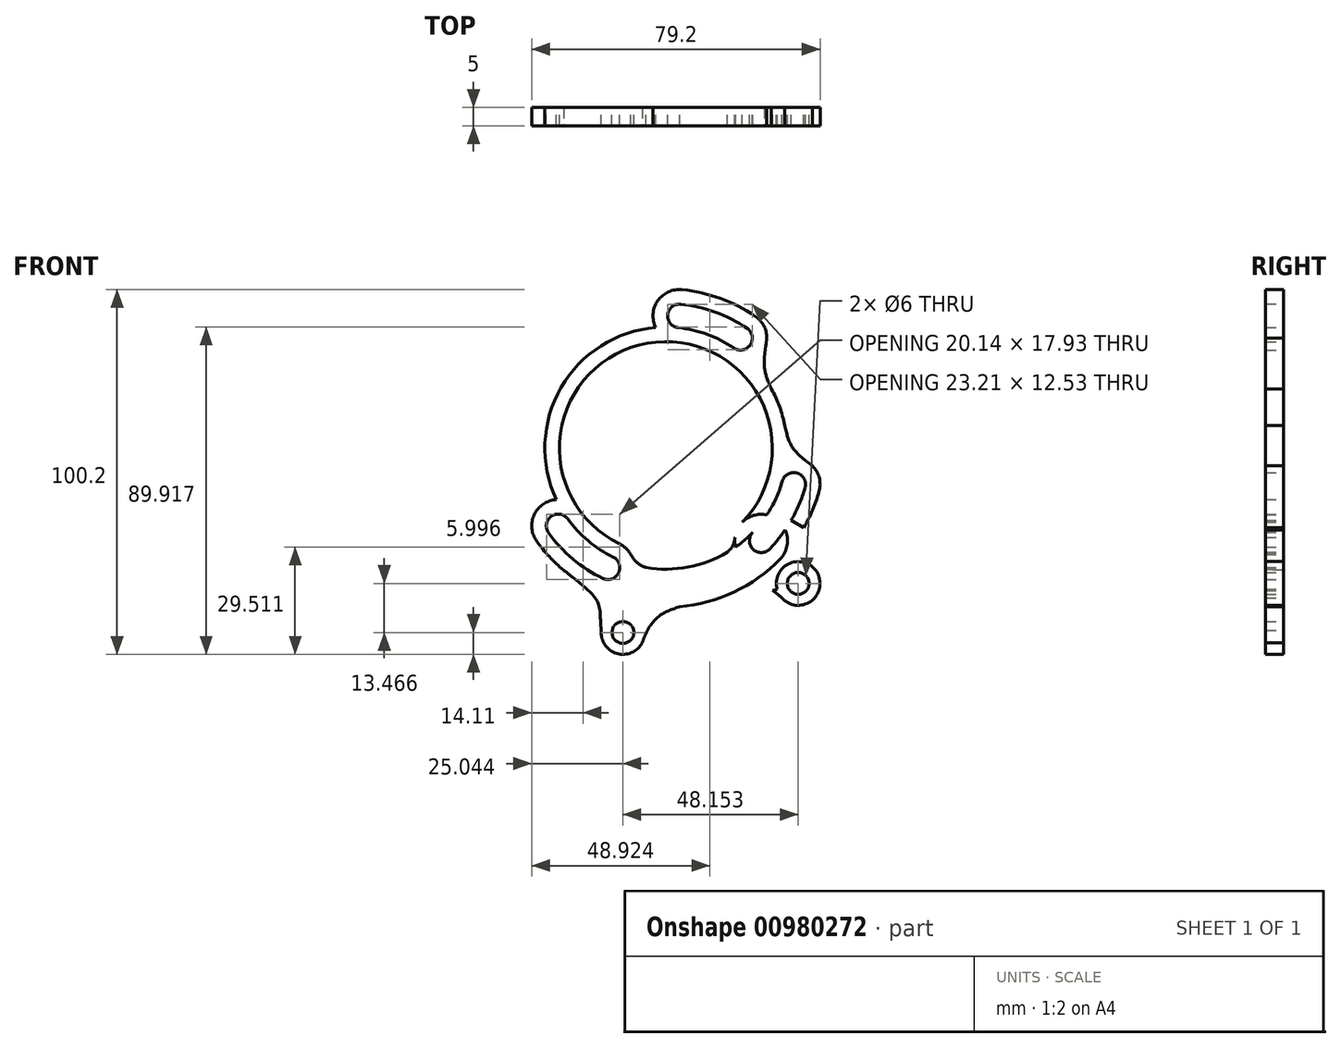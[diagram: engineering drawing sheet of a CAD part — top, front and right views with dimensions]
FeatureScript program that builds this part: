
annotation { "Feature Type Name" : "Feature", "Feature Type Description" : "" }
export const myFeature = defineFeature(function(context is Context, id is Id, definition is map)
    precondition{}
    {
        {
            var Q0;
            Q0=qCreatedBy(makeId("Front.planeOp"),FACE);
            var sketch = newSketch(context, id + "F0", { "sketchPlane" : qUnion([Q0])});
            skCircle(sketch, "E0", {"center": v(0, 0) * mm, "radius": 36.5 * mm});
            skCircle(sketch, "E1", {"center": v(-23.46, -27.96) * mm, "radius": 3.25 * mm});
            skCircle(sketch, "E2", {"center": v(31.6, -18.25) * mm, "radius": 3.25 * mm});
            skCircle(sketch, "E3", {"center": v(12.48, 34.3) * mm, "radius": 3.25 * mm});
            skLineSegment(sketch, "E4", {"start": v(0, 0) * mm, "end": v(-38.76, -46.2) * mm});
            skLineSegment(sketch, "E5", {"start": v(-38.76, -46.2) * mm, "end": v(0, 0) * mm});
            skLineSegment(sketch, "E6", {"start": v(0, 0) * mm, "end": v(58.35, -33.69) * mm});
            skLineSegment(sketch, "E7", {"start": v(58.35, -33.69) * mm, "end": v(0, 0) * mm});
            skLineSegment(sketch, "E8", {"start": v(0, 0) * mm, "end": v(16.1, 44.25) * mm});
            skCircle(sketch, "E9", {"center": v(3.71, 36.31) * mm, "radius": 3.25 * mm});
            skCircle(sketch, "E10", {"center": v(20.5, 30.2) * mm, "radius": 3.25 * mm});
            skCircle(sketch, "E11", {"center": v(35.11, -9.96) * mm, "radius": 3.25 * mm});
            skCircle(sketch, "E12", {"center": v(26.18, -25.43) * mm, "radius": 3.25 * mm});
            skCircle(sketch, "E13", {"center": v(-15.9, -32.85) * mm, "radius": 3.25 * mm});
            skCircle(sketch, "E14", {"center": v(-29.6, -21.37) * mm, "radius": 3.25 * mm});
            skLineSegment(sketch, "E15", {"start": v(-29.6, -21.37) * mm, "end": v(-23.46, -27.96) * mm});
            skLineSegment(sketch, "E16", {"start": v(-23.46, -27.96) * mm, "end": v(-15.9, -32.85) * mm});
            skLineSegment(sketch, "E17", {"start": v(26.18, -25.43) * mm, "end": v(31.6, -18.25) * mm});
            skLineSegment(sketch, "E18", {"start": v(35.11, -9.96) * mm, "end": v(31.6, -18.25) * mm});
            skLineSegment(sketch, "E19", {"start": v(12.48, 34.3) * mm, "end": v(20.5, 30.2) * mm});
            skLineSegment(sketch, "E20", {"start": v(12.48, 34.3) * mm, "end": v(3.71, 36.31) * mm});
            skCircle(sketch, "E21", {"center": v(0, 0) * mm, "radius": 33.25 * mm});
            skCircle(sketch, "E22", {"center": v(0, 0) * mm, "radius": 39.75 * mm});
            skCircle(sketch, "E23", {"center": v(0, 0) * mm, "radius": 29.25 * mm});
            skCircle(sketch, "E24", {"center": v(0, 0) * mm, "radius": 43.75 * mm});
            skCircle(sketch, "E25", {"center": v(3.71, 36.31) * mm, "radius": 7.25 * mm});
            skCircle(sketch, "E26", {"center": v(-29.6, -21.37) * mm, "radius": 7.25 * mm});
            skCircle(sketch, "E27", {"center": v(-15.9, -32.85) * mm, "radius": 7.25 * mm});
            skCircle(sketch, "E28", {"center": v(26.18, -25.43) * mm, "radius": 7.25 * mm});
            skCircle(sketch, "E29", {"center": v(35.11, -9.96) * mm, "radius": 7.25 * mm});
            skCircle(sketch, "E30", {"center": v(20.5, 30.2) * mm, "radius": 7.25 * mm});
            skCircle(sketch, "E31", {"center": v(0, 0) * mm, "radius": 52 * mm});
            skCircle(sketch, "E32", {"center": v(-11.8, -50.64) * mm, "radius": 3 * mm});
            skCircle(sketch, "E33", {"center": v(-11.8, -50.64) * mm, "radius": 6 * mm});
            skCircle(sketch, "E34", {"center": v(36.36, -37.18) * mm, "radius": 3 * mm});
            skCircle(sketch, "E35", {"center": v(36.36, -37.18) * mm, "radius": 6 * mm});
            skLineSegment(sketch, "E36", {"start": v(-11.8, -50.64) * mm, "end": v(36.36, -37.18) * mm});
            skFitSpline(sketch, "E37", {"points": [v(-17.77, -50.08) * mm, v(-28.12, -33.51) * mm], "startDerivative": vector(-2.15, 24.86) * mm, "endDerivative": vector(-34.83, 26.96) * mm});
            skFitSpline(sketch, "E38", {"points": [v(-6.5, -53.46) * mm, v(3.76, -43.59) * mm], "startDerivative": vector(7, 19.86) * mm, "endDerivative": vector(16.08, 4.93) * mm});
            skFitSpline(sketch, "E39", {"points": [v(31.83, -41.12) * mm, v(20.07, -38.88) * mm], "startDerivative": vector(-11.97, 10.58) * mm, "endDerivative": vector(-20.52, -5.17) * mm});
            skFitSpline(sketch, "E40", {"points": [v(40.4, -32.74) * mm, v(39.4, -19) * mm], "startDerivative": vector(-8.21, 10.84) * mm, "endDerivative": vector(10.07, 24.3) * mm});
            skFitSpline(sketch, "E41", {"points": [v(-9.62, -29.24) * mm, v(-5.43, -32.8) * mm], "startDerivative": vector(3.56, -5.9) * mm, "endDerivative": vector(6.8, -2.28) * mm});
            skFitSpline(sketch, "E42", {"points": [v(19, -24.5) * mm, v(16.88, -28.65) * mm], "startDerivative": vector(-0.78, -6.28) * mm, "endDerivative": vector(-4.07, -3.91) * mm});
            skFitSpline(sketch, "E43", {"points": [v(27.75, 30.27) * mm, v(29, 16.25) * mm], "startDerivative": vector(-3.36, -22.5) * mm, "endDerivative": vector(7.15, -15.45) * mm});
            skFitSpline(sketch, "E44", {"points": [v(40.2, -4.8) * mm, v(32.67, 6.19) * mm], "startDerivative": vector(-16.22, 11.75) * mm, "endDerivative": vector(-3.55, 16.52) * mm});
            skCircle(sketch, "E45", {"center": v(0, 0) * mm, "radius": 63 * mm});
            skCircle(sketch, "E46", {"center": v(6.41, -62.67) * mm, "radius": 3 * mm});
            skCircle(sketch, "E47", {"center": v(6.41, -62.67) * mm, "radius": 6 * mm});
            skCircle(sketch, "E48", {"center": v(50.05, -38.26) * mm, "radius": 3 * mm});
            skCircle(sketch, "E49", {"center": v(50.05, -38.26) * mm, "radius": 6 * mm});
            skLineSegment(sketch, "E50", {"start": v(6.41, -62.67) * mm, "end": v(50.05, -38.26) * mm});
            skSolve(sketch);
        }
        {
            var Q0;
            {var subQ0=sQuery(id+"F0.wireOp",EDGE,"E22");var subQ1=makeQuery(id+"F0.imprint","INTERSECT",VERTEX,{"derivedFrom":[sQuery(id+"F0.wireOp",EDGE,"E14"),subQ0]});Q0=makeQuery(id+"F0.imprint","IMPRINT",FACE,{"disambiguationData":[TD([[makeQuery(id+"F0.imprint","IMPRINT",EDGE,{"disambiguationData":[TD([[subQ1,1.0]])],"derivedFrom":subQ0}),-1.0]])]});}
            var Q1;
            {var subQ0=sQuery(id+"F0.wireOp",EDGE,"E26");var subQ1=sQuery(id+"F0.wireOp",EDGE,"E0");var subQ2=makeQuery(id+"F0.imprint","INTERSECT",VERTEX,{"disambiguationData":[OD(0.0)],"derivedFrom":[subQ1,subQ0]});Q1=makeQuery(id+"F0.imprint","IMPRINT",FACE,{"disambiguationData":[TD([[makeQuery(id+"F0.imprint","IMPRINT",EDGE,{"disambiguationData":[TD([[subQ2,-1.0]])],"derivedFrom":subQ1}),-1.0]])]});}
            var Q2;
            {var subQ0=sQuery(id+"F0.wireOp",EDGE,"E26");var subQ1=sQuery(id+"F0.wireOp",EDGE,"E0");var subQ2=makeQuery(id+"F0.imprint","INTERSECT",VERTEX,{"disambiguationData":[OD(0.0)],"derivedFrom":[subQ1,subQ0]});Q2=makeQuery(id+"F0.imprint","IMPRINT",FACE,{"disambiguationData":[TD([[makeQuery(id+"F0.imprint","IMPRINT",EDGE,{"disambiguationData":[TD([[subQ2,-1.0]])],"derivedFrom":subQ1}),1.0]])]});}
            var Q3;
            {var subQ0=sQuery(id+"F0.wireOp",EDGE,"E21");var subQ1=makeQuery(id+"F0.imprint","INTERSECT",VERTEX,{"derivedFrom":[sQuery(id+"F0.wireOp",EDGE,"E14"),subQ0]});Q3=makeQuery(id+"F0.imprint","IMPRINT",FACE,{"disambiguationData":[TD([[makeQuery(id+"F0.imprint","IMPRINT",EDGE,{"disambiguationData":[TD([[subQ1,1.0]])],"derivedFrom":subQ0}),1.0]])]});}
            var Q4;
            {var subQ0=sQuery(id+"F0.wireOp",EDGE,"E23");var subQ1=sQuery(id+"F0.wireOp",EDGE,"E5");var subQ2=makeQuery(id+"F0.imprint","INTERSECT",VERTEX,{"derivedFrom":[subQ1,subQ0]});Q4=makeQuery(id+"F0.imprint","IMPRINT",FACE,{"disambiguationData":[TD([[makeQuery(id+"F0.imprint","IMPRINT",EDGE,{"disambiguationData":[TD([[subQ2,1.0]])],"derivedFrom":subQ0}),-1.0]])]});}
            var Q5;
            {var subQ0=sQuery(id+"F0.wireOp",EDGE,"E23");var subQ1=sQuery(id+"F0.wireOp",EDGE,"E5");var subQ2=makeQuery(id+"F0.imprint","INTERSECT",VERTEX,{"derivedFrom":[subQ1,subQ0]});Q5=makeQuery(id+"F0.imprint","IMPRINT",FACE,{"disambiguationData":[TD([[makeQuery(id+"F0.imprint","IMPRINT",EDGE,{"disambiguationData":[TD([[subQ2,-1.0]])],"derivedFrom":subQ0}),-1.0]])]});}
            var Q6;
            {var subQ3=sQuery(id+"F0.wireOp",EDGE,"E21");var subQ5=makeQuery(id+"F0.imprint","INTERSECT",VERTEX,{"derivedFrom":[sQuery(id+"F0.wireOp",EDGE,"E13"),subQ3]});Q6=makeQuery(id+"F0.imprint","IMPRINT",FACE,{"disambiguationData":[TD([[makeQuery(id+"F0.imprint","IMPRINT",EDGE,{"disambiguationData":[TD([[subQ5,1.0]])],"derivedFrom":subQ3}),1.0]])]});}
            var Q7;
            {var subQ0=sQuery(id+"F0.wireOp",EDGE,"E41");Q7=makeQuery(id+"F0.imprint","IMPRINT",FACE,{"disambiguationData":[TD([[makeQuery(id+"F0.imprint","IMPRINT",EDGE,{"derivedFrom":subQ0}),-1.0]])]});}
            var Q8;
            {var subQ3=sQuery(id+"F0.wireOp",EDGE,"E22");var subQ5=sQuery(id+"F0.wireOp",EDGE,"E26");var subQ6=makeQuery(id+"F0.imprint","INTERSECT",VERTEX,{"disambiguationData":[OD(1.0)],"derivedFrom":[subQ3,subQ5]});Q8=makeQuery(id+"F0.imprint","IMPRINT",FACE,{"disambiguationData":[TD([[makeQuery(id+"F0.imprint","IMPRINT",EDGE,{"disambiguationData":[TD([[subQ6,1.0]])],"derivedFrom":subQ5}),-1.0]])]});}
            var Q9;
            {var subQ3=sQuery(id+"F0.wireOp",EDGE,"E22");var subQ5=sQuery(id+"F0.wireOp",EDGE,"E27");var subQ6=makeQuery(id+"F0.imprint","INTERSECT",VERTEX,{"disambiguationData":[OD(0.0)],"derivedFrom":[subQ3,subQ5]});Q9=makeQuery(id+"F0.imprint","IMPRINT",FACE,{"disambiguationData":[TD([[makeQuery(id+"F0.imprint","IMPRINT",EDGE,{"disambiguationData":[TD([[subQ6,-1.0]])],"derivedFrom":subQ5}),-1.0]])]});}
            var Q10;
            {var subQ0=sQuery(id+"F0.wireOp",EDGE,"E33");var subQ1=sQuery(id+"F0.wireOp",EDGE,"E31");var subQ2=makeQuery(id+"F0.imprint","INTERSECT",VERTEX,{"disambiguationData":[OD(0.0)],"derivedFrom":[subQ1,subQ0]});Q10=makeQuery(id+"F0.imprint","IMPRINT",FACE,{"disambiguationData":[TD([[makeQuery(id+"F0.imprint","IMPRINT",EDGE,{"disambiguationData":[TD([[subQ2,-1.0]])],"derivedFrom":subQ1}),1.0]])]});}
            var Q11;
            {var subQ0=sQuery(id+"F0.wireOp",EDGE,"E33");var subQ2=sQuery(id+"F0.wireOp",EDGE,"E31");var subQ3=makeQuery(id+"F0.imprint","INTERSECT",VERTEX,{"disambiguationData":[OD(0.0)],"derivedFrom":[subQ2,subQ0]});Q11=makeQuery(id+"F0.imprint","IMPRINT",FACE,{"disambiguationData":[TD([[makeQuery(id+"F0.imprint","IMPRINT",EDGE,{"disambiguationData":[TD([[subQ3,-1.0]])],"derivedFrom":subQ2}),-1.0]])]});}
            var Q12;
            {var subQ0=sQuery(id+"F0.wireOp",EDGE,"E32");var subQ1=sQuery(id+"F0.wireOp",EDGE,"E31");var subQ2=makeQuery(id+"F0.imprint","INTERSECT",VERTEX,{"disambiguationData":[OD(1.0)],"derivedFrom":[subQ1,subQ0]});Q12=makeQuery(id+"F0.imprint","IMPRINT",FACE,{"disambiguationData":[TD([[makeQuery(id+"F0.imprint","IMPRINT",EDGE,{"disambiguationData":[TD([[subQ2,-1.0]])],"derivedFrom":subQ1}),1.0]])]});}
            var Q13;
            {var subQ5=sQuery(id+"F0.wireOp",EDGE,"E38");var subQ6=sQuery(id+"F0.wireOp",EDGE,"E24");var subQ7=makeQuery(id+"F0.imprint","INTERSECT",VERTEX,{"derivedFrom":[subQ6,subQ5]});Q13=makeQuery(id+"F0.imprint","IMPRINT",FACE,{"disambiguationData":[TD([[makeQuery(id+"F0.imprint","IMPRINT",EDGE,{"disambiguationData":[TD([[subQ7,1.0]])],"derivedFrom":subQ6}),-1.0]])]});}
            var Q14;
            {var subQ0=sQuery(id+"F0.wireOp",EDGE,"E37");var subQ1=sQuery(id+"F0.wireOp",EDGE,"E31");var subQ2=makeQuery(id+"F0.imprint","INTERSECT",VERTEX,{"derivedFrom":[subQ1,subQ0]});Q14=makeQuery(id+"F0.imprint","IMPRINT",FACE,{"disambiguationData":[TD([[makeQuery(id+"F0.imprint","IMPRINT",EDGE,{"disambiguationData":[TD([[subQ2,-1.0]])],"derivedFrom":subQ1}),-1.0]])]});}
            var Q15;
            {var subQ0=sQuery(id+"F0.wireOp",EDGE,"E38");var subQ1=sQuery(id+"F0.wireOp",EDGE,"E31");var subQ2=makeQuery(id+"F0.imprint","INTERSECT",VERTEX,{"derivedFrom":[subQ1,subQ0]});Q15=makeQuery(id+"F0.imprint","IMPRINT",FACE,{"disambiguationData":[TD([[makeQuery(id+"F0.imprint","IMPRINT",EDGE,{"disambiguationData":[TD([[subQ2,1.0]])],"derivedFrom":subQ1}),-1.0]])]});}
            var Q16;
            {var subQ0=sQuery(id+"F0.wireOp",EDGE,"E38");var subQ1=sQuery(id+"F0.wireOp",EDGE,"E31");var subQ2=makeQuery(id+"F0.imprint","INTERSECT",VERTEX,{"derivedFrom":[subQ1,subQ0]});Q16=makeQuery(id+"F0.imprint","IMPRINT",FACE,{"disambiguationData":[TD([[makeQuery(id+"F0.imprint","IMPRINT",EDGE,{"disambiguationData":[TD([[subQ2,1.0]])],"derivedFrom":subQ1}),1.0]])]});}
            var Q17;
            {var subQ3=sQuery(id+"F0.wireOp",EDGE,"E27");var subQ7=sQuery(id+"F0.wireOp",EDGE,"E22");var subQ8=makeQuery(id+"F0.imprint","INTERSECT",VERTEX,{"disambiguationData":[OD(1.0)],"derivedFrom":[subQ7,subQ3]});Q17=makeQuery(id+"F0.imprint","IMPRINT",FACE,{"disambiguationData":[TD([[makeQuery(id+"F0.imprint","IMPRINT",EDGE,{"disambiguationData":[TD([[subQ8,-1.0]])],"derivedFrom":subQ7}),-1.0]])]});}
            var Q18;
            {var subQ0=sQuery(id+"F0.wireOp",EDGE,"E22");var subQ1=makeQuery(id+"F0.imprint","INTERSECT",VERTEX,{"derivedFrom":[sQuery(id+"F0.wireOp",EDGE,"E13"),subQ0]});Q18=makeQuery(id+"F0.imprint","IMPRINT",FACE,{"disambiguationData":[TD([[makeQuery(id+"F0.imprint","IMPRINT",EDGE,{"disambiguationData":[TD([[subQ1,1.0]])],"derivedFrom":subQ0}),-1.0]])]});}
            var Q19;
            {var subQ5=sQuery(id+"F0.wireOp",EDGE,"E27");var subQ7=sQuery(id+"F0.wireOp",EDGE,"E0");var subQ8=makeQuery(id+"F0.imprint","INTERSECT",VERTEX,{"disambiguationData":[OD(1.0)],"derivedFrom":[subQ7,subQ5]});Q19=makeQuery(id+"F0.imprint","IMPRINT",FACE,{"disambiguationData":[TD([[makeQuery(id+"F0.imprint","IMPRINT",EDGE,{"disambiguationData":[TD([[subQ8,-1.0]])],"derivedFrom":subQ7}),1.0]])]});}
            var Q20;
            {var subQ0=sQuery(id+"F0.wireOp",EDGE,"E27");var subQ1=sQuery(id+"F0.wireOp",EDGE,"E0");var subQ2=makeQuery(id+"F0.imprint","INTERSECT",VERTEX,{"disambiguationData":[OD(1.0)],"derivedFrom":[subQ1,subQ0]});Q20=makeQuery(id+"F0.imprint","IMPRINT",FACE,{"disambiguationData":[TD([[makeQuery(id+"F0.imprint","IMPRINT",EDGE,{"disambiguationData":[TD([[subQ2,-1.0]])],"derivedFrom":subQ1}),-1.0]])]});}
            var Q21;
            {var subQ0=sQuery(id+"F0.wireOp",EDGE,"E13");var subQ1=sQuery(id+"F0.wireOp",EDGE,"E0");var subQ2=makeQuery(id+"F0.imprint","INTERSECT",VERTEX,{"disambiguationData":[OD(1.0)],"derivedFrom":[subQ1,subQ0]});Q21=makeQuery(id+"F0.imprint","IMPRINT",FACE,{"disambiguationData":[TD([[makeQuery(id+"F0.imprint","IMPRINT",EDGE,{"disambiguationData":[TD([[subQ2,-1.0]])],"derivedFrom":subQ1}),1.0]])]});}
            var Q22;
            {var subQ0=sQuery(id+"F0.wireOp",EDGE,"E13");var subQ1=sQuery(id+"F0.wireOp",EDGE,"E0");var subQ2=makeQuery(id+"F0.imprint","INTERSECT",VERTEX,{"disambiguationData":[OD(1.0)],"derivedFrom":[subQ1,subQ0]});Q22=makeQuery(id+"F0.imprint","IMPRINT",FACE,{"disambiguationData":[TD([[makeQuery(id+"F0.imprint","IMPRINT",EDGE,{"disambiguationData":[TD([[subQ2,-1.0]])],"derivedFrom":subQ1}),-1.0]])]});}
            var Q23;
            {var subQ0=sQuery(id+"F0.wireOp",EDGE,"E40");var subQ6=sQuery(id+"F0.wireOp",EDGE,"E7");var subQ11=makeQuery(id+"F0.imprint","INTERSECT",VERTEX,{"derivedFrom":[subQ6,subQ0]});Q23=makeQuery(id+"F0.imprint","IMPRINT",FACE,{"disambiguationData":[TD([[makeQuery(id+"F0.imprint","IMPRINT",EDGE,{"disambiguationData":[TD([[subQ11,-1.0]])],"derivedFrom":subQ6}),1.0]])]});}
            var Q24;
            {var subQ0=sQuery(id+"F0.wireOp",EDGE,"E42");Q24=makeQuery(id+"F0.imprint","IMPRINT",FACE,{"disambiguationData":[TD([[makeQuery(id+"F0.imprint","IMPRINT",EDGE,{"derivedFrom":subQ0}),1.0]])]});}
            var Q25;
            {var subQ0=sQuery(id+"F0.wireOp",EDGE,"E28");var subQ1=makeQuery(id+"F0.imprint","IMPRINT",VERTEX,{"derivedFrom":subQ0});Q25=makeQuery(id+"F0.imprint","IMPRINT",FACE,{"disambiguationData":[TD([[makeQuery(id+"F0.imprint","IMPRINT",EDGE,{"disambiguationData":[TD([[subQ1,1.0]])],"derivedFrom":subQ0}),1.0]])]});}
            var Q26;
            {var subQ0=sQuery(id+"F0.wireOp",EDGE,"E28");var subQ1=sQuery(id+"F0.wireOp",EDGE,"E0");var subQ2=makeQuery(id+"F0.imprint","INTERSECT",VERTEX,{"disambiguationData":[OD(0.0)],"derivedFrom":[subQ1,subQ0]});Q26=makeQuery(id+"F0.imprint","IMPRINT",FACE,{"disambiguationData":[TD([[makeQuery(id+"F0.imprint","IMPRINT",EDGE,{"disambiguationData":[TD([[subQ2,-1.0]])],"derivedFrom":subQ1}),1.0]])]});}
            var Q27;
            {var subQ0=sQuery(id+"F0.wireOp",EDGE,"E28");var subQ1=sQuery(id+"F0.wireOp",EDGE,"E0");var subQ2=makeQuery(id+"F0.imprint","INTERSECT",VERTEX,{"disambiguationData":[OD(0.0)],"derivedFrom":[subQ1,subQ0]});Q27=makeQuery(id+"F0.imprint","IMPRINT",FACE,{"disambiguationData":[TD([[makeQuery(id+"F0.imprint","IMPRINT",EDGE,{"disambiguationData":[TD([[subQ2,-1.0]])],"derivedFrom":subQ1}),-1.0]])]});}
            var Q28;
            {var subQ0=sQuery(id+"F0.wireOp",EDGE,"E22");var subQ1=makeQuery(id+"F0.imprint","INTERSECT",VERTEX,{"derivedFrom":[sQuery(id+"F0.wireOp",EDGE,"E12"),subQ0]});Q28=makeQuery(id+"F0.imprint","IMPRINT",FACE,{"disambiguationData":[TD([[makeQuery(id+"F0.imprint","IMPRINT",EDGE,{"disambiguationData":[TD([[subQ1,1.0]])],"derivedFrom":subQ0}),-1.0]])]});}
            var Q29;
            {var subQ1=sQuery(id+"F0.wireOp",EDGE,"E31");var subQ3=sQuery(id+"F0.wireOp",EDGE,"E34");var subQ4=makeQuery(id+"F0.imprint","INTERSECT",VERTEX,{"disambiguationData":[OD(1.0)],"derivedFrom":[subQ1,subQ3]});Q29=makeQuery(id+"F0.imprint","IMPRINT",FACE,{"disambiguationData":[TD([[makeQuery(id+"F0.imprint","IMPRINT",EDGE,{"disambiguationData":[TD([[subQ4,-1.0]])],"derivedFrom":subQ3}),-1.0]])]});}
            var Q30;
            {var subQ1=sQuery(id+"F0.wireOp",EDGE,"E31");var subQ3=sQuery(id+"F0.wireOp",EDGE,"E34");var subQ4=makeQuery(id+"F0.imprint","INTERSECT",VERTEX,{"disambiguationData":[OD(0.0)],"derivedFrom":[subQ1,subQ3]});Q30=makeQuery(id+"F0.imprint","IMPRINT",FACE,{"disambiguationData":[TD([[makeQuery(id+"F0.imprint","IMPRINT",EDGE,{"disambiguationData":[TD([[subQ4,-1.0]])],"derivedFrom":subQ3}),-1.0]])]});}
            var Q31;
            {var subQ0=sQuery(id+"F0.wireOp",EDGE,"E24");var subQ1=sQuery(id+"F0.wireOp",EDGE,"E7");var subQ2=makeQuery(id+"F0.imprint","INTERSECT",VERTEX,{"derivedFrom":[subQ1,subQ0]});Q31=makeQuery(id+"F0.imprint","IMPRINT",FACE,{"disambiguationData":[TD([[makeQuery(id+"F0.imprint","IMPRINT",EDGE,{"disambiguationData":[TD([[subQ2,1.0]])],"derivedFrom":subQ0}),1.0]])]});}
            var Q32;
            {var subQ0=sQuery(id+"F0.wireOp",EDGE,"E24");var subQ1=makeQuery(id+"F0.imprint","INTERSECT",VERTEX,{"derivedFrom":[subQ0,sQuery(id+"F0.wireOp",EDGE,"E40")]});Q32=makeQuery(id+"F0.imprint","IMPRINT",FACE,{"disambiguationData":[TD([[makeQuery(id+"F0.imprint","IMPRINT",EDGE,{"disambiguationData":[TD([[subQ1,1.0]])],"derivedFrom":subQ0}),1.0]])]});}
            var Q33;
            {var subQ0=sQuery(id+"F0.wireOp",EDGE,"E23");var subQ1=sQuery(id+"F0.wireOp",EDGE,"E7");var subQ2=makeQuery(id+"F0.imprint","INTERSECT",VERTEX,{"derivedFrom":[subQ1,subQ0]});Q33=makeQuery(id+"F0.imprint","IMPRINT",FACE,{"disambiguationData":[TD([[makeQuery(id+"F0.imprint","IMPRINT",EDGE,{"disambiguationData":[TD([[subQ2,1.0]])],"derivedFrom":subQ0}),-1.0]])]});}
            var Q34;
            {var subQ0=sQuery(id+"F0.wireOp",EDGE,"E23");var subQ1=sQuery(id+"F0.wireOp",EDGE,"E7");var subQ2=makeQuery(id+"F0.imprint","INTERSECT",VERTEX,{"derivedFrom":[subQ1,subQ0]});Q34=makeQuery(id+"F0.imprint","IMPRINT",FACE,{"disambiguationData":[TD([[makeQuery(id+"F0.imprint","IMPRINT",EDGE,{"disambiguationData":[TD([[subQ2,-1.0]])],"derivedFrom":subQ0}),-1.0]])]});}
            var Q35;
            {var subQ1=sQuery(id+"F0.wireOp",EDGE,"E31");var subQ3=sQuery(id+"F0.wireOp",EDGE,"E34");var subQ4=makeQuery(id+"F0.imprint","INTERSECT",VERTEX,{"disambiguationData":[OD(0.0)],"derivedFrom":[subQ1,subQ3]});Q35=makeQuery(id+"F0.imprint","IMPRINT",FACE,{"disambiguationData":[TD([[makeQuery(id+"F0.imprint","IMPRINT",EDGE,{"disambiguationData":[TD([[subQ4,1.0]])],"derivedFrom":subQ3}),-1.0]])]});}
            var Q36;
            {var subQ1=sQuery(id+"F0.wireOp",EDGE,"E35");var subQ3=sQuery(id+"F0.wireOp",EDGE,"E36");var subQ4=makeQuery(id+"F0.imprint","INTERSECT",VERTEX,{"derivedFrom":[subQ1,subQ3]});Q36=makeQuery(id+"F0.imprint","IMPRINT",FACE,{"disambiguationData":[TD([[makeQuery(id+"F0.imprint","IMPRINT",EDGE,{"disambiguationData":[TD([[subQ4,1.0]])],"derivedFrom":subQ3}),-1.0]])]});}
            var Q37;
            {var subQ0=sQuery(id+"F0.wireOp",EDGE,"E40");var subQ1=sQuery(id+"F0.wireOp",EDGE,"E7");var subQ2=makeQuery(id+"F0.imprint","INTERSECT",VERTEX,{"derivedFrom":[subQ1,subQ0]});Q37=makeQuery(id+"F0.imprint","IMPRINT",FACE,{"disambiguationData":[TD([[makeQuery(id+"F0.imprint","IMPRINT",EDGE,{"disambiguationData":[TD([[subQ2,-1.0]])],"derivedFrom":subQ1}),-1.0]])]});}
            var Q38;
            {var subQ1=sQuery(id+"F0.wireOp",EDGE,"E22");var subQ8=makeQuery(id+"F0.imprint","INTERSECT",VERTEX,{"derivedFrom":[sQuery(id+"F0.wireOp",EDGE,"E11"),subQ1]});Q38=makeQuery(id+"F0.imprint","IMPRINT",FACE,{"disambiguationData":[TD([[makeQuery(id+"F0.imprint","IMPRINT",EDGE,{"disambiguationData":[TD([[subQ8,1.0]])],"derivedFrom":subQ1}),-1.0]])]});}
            var Q39;
            {var subQ0=sQuery(id+"F0.wireOp",EDGE,"E11");var subQ1=sQuery(id+"F0.wireOp",EDGE,"E0");var subQ2=makeQuery(id+"F0.imprint","INTERSECT",VERTEX,{"disambiguationData":[OD(1.0)],"derivedFrom":[subQ1,subQ0]});Q39=makeQuery(id+"F0.imprint","IMPRINT",FACE,{"disambiguationData":[TD([[makeQuery(id+"F0.imprint","IMPRINT",EDGE,{"disambiguationData":[TD([[subQ2,-1.0]])],"derivedFrom":subQ1}),-1.0]])]});}
            var Q40;
            {var subQ0=sQuery(id+"F0.wireOp",EDGE,"E11");var subQ1=sQuery(id+"F0.wireOp",EDGE,"E0");var subQ2=makeQuery(id+"F0.imprint","INTERSECT",VERTEX,{"disambiguationData":[OD(1.0)],"derivedFrom":[subQ1,subQ0]});Q40=makeQuery(id+"F0.imprint","IMPRINT",FACE,{"disambiguationData":[TD([[makeQuery(id+"F0.imprint","IMPRINT",EDGE,{"disambiguationData":[TD([[subQ2,-1.0]])],"derivedFrom":subQ1}),1.0]])]});}
            var Q41;
            {var subQ0=sQuery(id+"F0.wireOp",EDGE,"E21");var subQ1=makeQuery(id+"F0.imprint","INTERSECT",VERTEX,{"derivedFrom":[sQuery(id+"F0.wireOp",EDGE,"E11"),subQ0]});Q41=makeQuery(id+"F0.imprint","IMPRINT",FACE,{"disambiguationData":[TD([[makeQuery(id+"F0.imprint","IMPRINT",EDGE,{"disambiguationData":[TD([[subQ1,1.0]])],"derivedFrom":subQ0}),1.0]])]});}
            var Q42;
            {var subQ0=sQuery(id+"F0.wireOp",EDGE,"E30");var subQ1=sQuery(id+"F0.wireOp",EDGE,"E21");var subQ2=makeQuery(id+"F0.imprint","INTERSECT",VERTEX,{"disambiguationData":[OD(0.0)],"derivedFrom":[subQ1,subQ0]});Q42=makeQuery(id+"F0.imprint","IMPRINT",FACE,{"disambiguationData":[TD([[makeQuery(id+"F0.imprint","IMPRINT",EDGE,{"disambiguationData":[TD([[subQ2,1.0]])],"derivedFrom":subQ1}),1.0]])]});}
            var Q43;
            {var subQ2=sQuery(id+"F0.wireOp",EDGE,"E22");var subQ6=makeQuery(id+"F0.imprint","INTERSECT",VERTEX,{"derivedFrom":[sQuery(id+"F0.wireOp",EDGE,"E10"),subQ2]});Q43=makeQuery(id+"F0.imprint","IMPRINT",FACE,{"disambiguationData":[TD([[makeQuery(id+"F0.imprint","IMPRINT",EDGE,{"disambiguationData":[TD([[subQ6,1.0]])],"derivedFrom":subQ2}),-1.0]])]});}
            var Q44;
            {var subQ0=sQuery(id+"F0.wireOp",EDGE,"E30");var subQ1=sQuery(id+"F0.wireOp",EDGE,"E0");var subQ2=makeQuery(id+"F0.imprint","INTERSECT",VERTEX,{"disambiguationData":[OD(0.0)],"derivedFrom":[subQ1,subQ0]});Q44=makeQuery(id+"F0.imprint","IMPRINT",FACE,{"disambiguationData":[TD([[makeQuery(id+"F0.imprint","IMPRINT",EDGE,{"disambiguationData":[TD([[subQ2,-1.0]])],"derivedFrom":subQ1}),-1.0]])]});}
            var Q45;
            {var subQ0=sQuery(id+"F0.wireOp",EDGE,"E30");var subQ1=sQuery(id+"F0.wireOp",EDGE,"E0");var subQ2=makeQuery(id+"F0.imprint","INTERSECT",VERTEX,{"disambiguationData":[OD(0.0)],"derivedFrom":[subQ1,subQ0]});Q45=makeQuery(id+"F0.imprint","IMPRINT",FACE,{"disambiguationData":[TD([[makeQuery(id+"F0.imprint","IMPRINT",EDGE,{"disambiguationData":[TD([[subQ2,-1.0]])],"derivedFrom":subQ1}),1.0]])]});}
            var Q46;
            {var subQ0=sQuery(id+"F0.wireOp",EDGE,"E21");var subQ1=makeQuery(id+"F0.imprint","INTERSECT",VERTEX,{"derivedFrom":[sQuery(id+"F0.wireOp",EDGE,"E10"),subQ0]});Q46=makeQuery(id+"F0.imprint","IMPRINT",FACE,{"disambiguationData":[TD([[makeQuery(id+"F0.imprint","IMPRINT",EDGE,{"disambiguationData":[TD([[subQ1,1.0]])],"derivedFrom":subQ0}),1.0]])]});}
            var Q47;
            {var subQ0=sQuery(id+"F0.wireOp",EDGE,"E23");var subQ1=sQuery(id+"F0.wireOp",EDGE,"E8");var subQ2=makeQuery(id+"F0.imprint","INTERSECT",VERTEX,{"derivedFrom":[subQ1,subQ0]});Q47=makeQuery(id+"F0.imprint","IMPRINT",FACE,{"disambiguationData":[TD([[makeQuery(id+"F0.imprint","IMPRINT",EDGE,{"disambiguationData":[TD([[subQ2,1.0]])],"derivedFrom":subQ0}),-1.0]])]});}
            var Q48;
            {var subQ0=sQuery(id+"F0.wireOp",EDGE,"E23");var subQ1=sQuery(id+"F0.wireOp",EDGE,"E8");var subQ2=makeQuery(id+"F0.imprint","INTERSECT",VERTEX,{"derivedFrom":[subQ1,subQ0]});Q48=makeQuery(id+"F0.imprint","IMPRINT",FACE,{"disambiguationData":[TD([[makeQuery(id+"F0.imprint","IMPRINT",EDGE,{"disambiguationData":[TD([[subQ2,-1.0]])],"derivedFrom":subQ0}),-1.0]])]});}
            var Q49;
            {var subQ0=sQuery(id+"F0.wireOp",EDGE,"E21");var subQ1=makeQuery(id+"F0.imprint","INTERSECT",VERTEX,{"derivedFrom":[sQuery(id+"F0.wireOp",EDGE,"E9"),subQ0]});Q49=makeQuery(id+"F0.imprint","IMPRINT",FACE,{"disambiguationData":[TD([[makeQuery(id+"F0.imprint","IMPRINT",EDGE,{"disambiguationData":[TD([[subQ1,1.0]])],"derivedFrom":subQ0}),1.0]])]});}
            var Q50;
            {var subQ0=sQuery(id+"F0.wireOp",EDGE,"E9");var subQ1=sQuery(id+"F0.wireOp",EDGE,"E0");var subQ2=makeQuery(id+"F0.imprint","INTERSECT",VERTEX,{"disambiguationData":[OD(1.0)],"derivedFrom":[subQ1,subQ0]});Q50=makeQuery(id+"F0.imprint","IMPRINT",FACE,{"disambiguationData":[TD([[makeQuery(id+"F0.imprint","IMPRINT",EDGE,{"disambiguationData":[TD([[subQ2,-1.0]])],"derivedFrom":subQ1}),1.0]])]});}
            var Q51;
            {var subQ0=sQuery(id+"F0.wireOp",EDGE,"E9");var subQ1=sQuery(id+"F0.wireOp",EDGE,"E0");var subQ2=makeQuery(id+"F0.imprint","INTERSECT",VERTEX,{"disambiguationData":[OD(1.0)],"derivedFrom":[subQ1,subQ0]});Q51=makeQuery(id+"F0.imprint","IMPRINT",FACE,{"disambiguationData":[TD([[makeQuery(id+"F0.imprint","IMPRINT",EDGE,{"disambiguationData":[TD([[subQ2,-1.0]])],"derivedFrom":subQ1}),-1.0]])]});}
            var Q52;
            {var subQ0=sQuery(id+"F0.wireOp",EDGE,"E22");var subQ1=makeQuery(id+"F0.imprint","INTERSECT",VERTEX,{"derivedFrom":[sQuery(id+"F0.wireOp",EDGE,"E9"),subQ0]});Q52=makeQuery(id+"F0.imprint","IMPRINT",FACE,{"disambiguationData":[TD([[makeQuery(id+"F0.imprint","IMPRINT",EDGE,{"disambiguationData":[TD([[subQ1,1.0]])],"derivedFrom":subQ0}),-1.0]])]});}
            var Q53;
            {var subQ0=sQuery(id+"F0.wireOp",EDGE,"E24");var subQ1=sQuery(id+"F0.wireOp",EDGE,"E8");var subQ2=makeQuery(id+"F0.imprint","INTERSECT",VERTEX,{"derivedFrom":[subQ1,subQ0]});Q53=makeQuery(id+"F0.imprint","IMPRINT",FACE,{"disambiguationData":[TD([[makeQuery(id+"F0.imprint","IMPRINT",EDGE,{"disambiguationData":[TD([[subQ2,-1.0]])],"derivedFrom":subQ0}),1.0]])]});}
            var Q54;
            {var subQ0=sQuery(id+"F0.wireOp",EDGE,"E24");var subQ1=sQuery(id+"F0.wireOp",EDGE,"E8");var subQ2=makeQuery(id+"F0.imprint","INTERSECT",VERTEX,{"derivedFrom":[subQ1,subQ0]});Q54=makeQuery(id+"F0.imprint","IMPRINT",FACE,{"disambiguationData":[TD([[makeQuery(id+"F0.imprint","IMPRINT",EDGE,{"disambiguationData":[TD([[subQ2,1.0]])],"derivedFrom":subQ0}),1.0]])]});}
            var Q55;
            {var subQ0=sQuery(id+"F0.wireOp",EDGE,"E30");var subQ1=sQuery(id+"F0.wireOp",EDGE,"E0");var subQ2=makeQuery(id+"F0.imprint","INTERSECT",VERTEX,{"disambiguationData":[OD(0.0)],"derivedFrom":[subQ1,subQ0]});Q55=makeQuery(id+"F0.imprint","IMPRINT",FACE,{"disambiguationData":[TD([[makeQuery(id+"F0.imprint","IMPRINT",EDGE,{"disambiguationData":[TD([[subQ2,1.0]])],"derivedFrom":subQ1}),-1.0]])]});}
            var Q56;
            {var subQ0=sQuery(id+"F0.wireOp",EDGE,"E29");var subQ1=sQuery(id+"F0.wireOp",EDGE,"E0");var subQ2=makeQuery(id+"F0.imprint","INTERSECT",VERTEX,{"disambiguationData":[OD(1.0)],"derivedFrom":[subQ1,subQ0]});Q56=makeQuery(id+"F0.imprint","IMPRINT",FACE,{"disambiguationData":[TD([[makeQuery(id+"F0.imprint","IMPRINT",EDGE,{"disambiguationData":[TD([[subQ2,-1.0]])],"derivedFrom":subQ1}),1.0]])]});}
            var Q57;
            {var subQ0=sQuery(id+"F0.wireOp",EDGE,"E29");var subQ1=sQuery(id+"F0.wireOp",EDGE,"E0");var subQ2=makeQuery(id+"F0.imprint","INTERSECT",VERTEX,{"disambiguationData":[OD(1.0)],"derivedFrom":[subQ1,subQ0]});Q57=makeQuery(id+"F0.imprint","IMPRINT",FACE,{"disambiguationData":[TD([[makeQuery(id+"F0.imprint","IMPRINT",EDGE,{"disambiguationData":[TD([[subQ2,-1.0]])],"derivedFrom":subQ1}),-1.0]])]});}
            var Q58;
            {var subQ0=sQuery(id+"F0.wireOp",EDGE,"E30");var subQ1=sQuery(id+"F0.wireOp",EDGE,"E0");var subQ2=makeQuery(id+"F0.imprint","INTERSECT",VERTEX,{"disambiguationData":[OD(0.0)],"derivedFrom":[subQ1,subQ0]});Q58=makeQuery(id+"F0.imprint","IMPRINT",FACE,{"disambiguationData":[TD([[makeQuery(id+"F0.imprint","IMPRINT",EDGE,{"disambiguationData":[TD([[subQ2,1.0]])],"derivedFrom":subQ1}),1.0]])]});}
            extrude(context, id + "F1", {"entities" : qUnion([Q0, Q1, Q2, Q3, Q4, Q5, Q6, Q7, Q8, Q9, Q10, Q11, Q12, Q13, Q14, Q15, Q16, Q17, Q18, Q19, Q20, Q21, Q22, Q23, Q24, Q25, Q26, Q27, Q28, Q29, Q30, Q31, Q32, Q33, Q34, Q35, Q36, Q37, Q38, Q39, Q40, Q41, Q42, Q43, Q44, Q45, Q46, Q47, Q48, Q49, Q50, Q51, Q52, Q53, Q54, Q55, Q56, Q57, Q58]), "depth" : 5 * mm, "offsetDistance" : 25 * mm});
        }
    });
